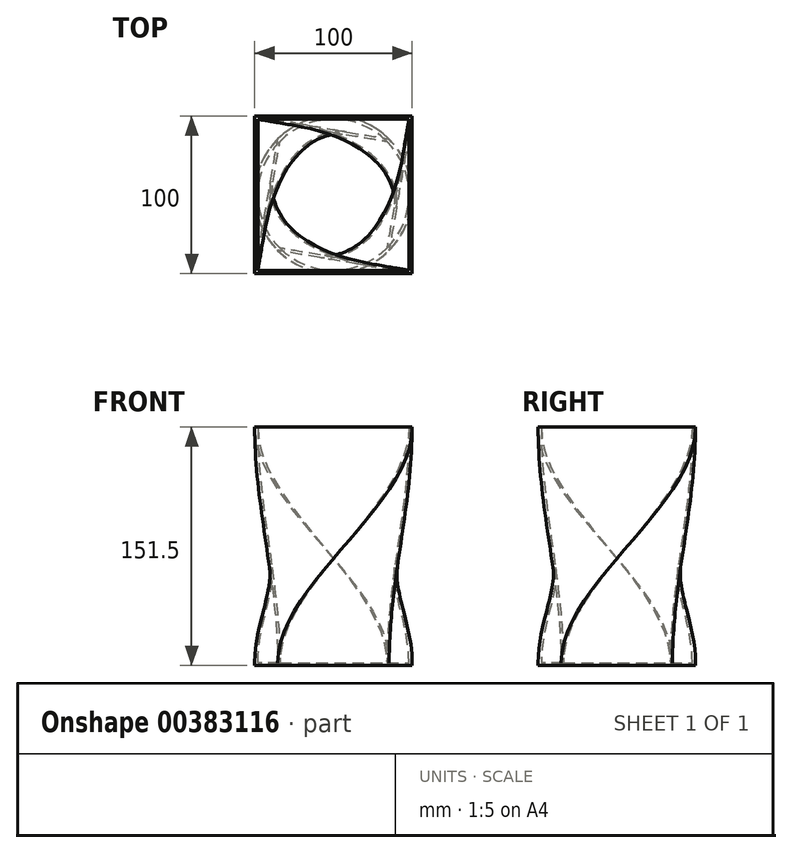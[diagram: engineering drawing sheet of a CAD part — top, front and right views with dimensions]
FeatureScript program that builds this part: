
annotation { "Feature Type Name" : "Feature", "Feature Type Description" : "" }
export const myFeature = defineFeature(function(context is Context, id is Id, definition is map)
    precondition{}
    {
        {
            var Q0;
            Q0=qCreatedBy(makeId("Top.planeOp"),FACE);
            var sketch = newSketch(context, id + "F0", { "sketchPlane" : qUnion([Q0])});
            skArc(sketch, "E0", {"start": v(35.36, 35.36) * mm, "mid": v(0, 50) * mm, "end": v(-35.36, 35.36) * mm});
            skArc(sketch, "E1", {"start": v(35.36, -35.36) * mm, "mid": v(50, 0) * mm, "end": v(35.36, 35.36) * mm});
            skArc(sketch, "E2", {"start": v(-35.36, -35.36) * mm, "mid": v(0, -50) * mm, "end": v(35.36, -35.36) * mm});
            skArc(sketch, "E3", {"start": v(-35.36, 35.36) * mm, "mid": v(-50, 0) * mm, "end": v(-35.36, -35.36) * mm});
            skLineSegment(sketch, "E4", {"start": v(0, 0) * mm, "end": v(51.34, 51.34) * mm, "construction": true});
            skLineSegment(sketch, "E5", {"start": v(0, 0) * mm, "end": v(45.23, -45.23) * mm, "construction": true});
            skLineSegment(sketch, "E6", {"start": v(0, 0) * mm, "end": v(-35.36, -35.36) * mm, "construction": true});
            skLineSegment(sketch, "E7", {"start": v(0, 0) * mm, "end": v(-35.36, 35.36) * mm, "construction": true});
            skSolve(sketch);
        }
        {
            var Q0;
            Q0=qCreatedBy(makeId("Top.planeOp"),FACE);
            cPlane(context, id + "F1", {"entities" : qUnion([Q0]), "cplaneType" : CPlaneType.OFFSET, "offset" : 150 * mm, "width" : 152.4 * mm, "height" : 152.4 * mm});
        }
        {
            var Q0;
            Q0=qCreatedBy(id+"F1.planeOp",FACE);
            var sketch = newSketch(context, id + "F2", { "sketchPlane" : qUnion([Q0])});
            skLineSegment(sketch, "E8.bottom", {"start": v(-50, 50) * mm, "end": v(50, 50) * mm});
            skLineSegment(sketch, "E8.top", {"start": v(-50, -50) * mm, "end": v(50, -50) * mm});
            skLineSegment(sketch, "E8.left", {"start": v(-50, 50) * mm, "end": v(-50, -50) * mm});
            skLineSegment(sketch, "E8.right", {"start": v(50, 50) * mm, "end": v(50, -50) * mm});
            skPoint(sketch, "E8.middle", {"position": v(0, 0) * mm});
            skSolve(sketch);
        }
        {
            var Q0;
            Q0=makeQuery(id+"F2.imprint","IMPRINT",FACE,{"disambiguationData":[TD([[makeQuery(id+"F2.imprint","IMPRINT",EDGE,{"derivedFrom":sQuery(id+"F2.wireOp",EDGE,"E8.bottom")}),-1.0]])]});
            var Q1;
            Q1=makeQuery(id+"F0.imprint","IMPRINT",FACE,{"disambiguationData":[TD([[makeQuery(id+"F0.imprint","IMPRINT",EDGE,{"derivedFrom":sQuery(id+"F0.wireOp",EDGE,"E0")}),1.0]])]});
            var Q2;
            Q2=sQuery(id+"F0.wireOp",VERTEX,"E6.end");
            var Q3;
            Q3=sQuery(id+"F2.wireOp",VERTEX,"E8.top.end");
            loft(context, id + "F3", {"startCondition" : LoftEndDerivativeType.NORMAL_TO_PROFILE, "startMagnitude" : 1, "endCondition" : LoftEndDerivativeType.NORMAL_TO_PROFILE, "endMagnitude" : 1, "sheetProfilesArray" : [{ "sheetProfileEntities" : qUnion([Q0]) }, { "sheetProfileEntities" : qUnion([Q1]) }], "matchConnections" : true, "connections" : [{ "connectionEntities" : qUnion([Q2, Q3]), "connectionEdgeQueries" : qUnion([]), "connectionEdgeParameters" : [] }]});
        }
        {
            var Q0;
            Q0=qCreatedBy(makeId("Top.planeOp"),FACE);
            var sketch = newSketch(context, id + "F4", { "sketchPlane" : qUnion([Q0])});
            skArc(sketch, "E9", {"start": v(33.94, 33.94) * mm, "mid": v(-33.94, 33.94) * mm, "end": v(-33.94, -33.94) * mm});
            skArc(sketch, "E10", {"start": v(33.94, -33.94) * mm, "mid": v(48, 0) * mm, "end": v(33.94, 33.94) * mm});
            skArc(sketch, "E11", {"start": v(-33.94, -33.94) * mm, "mid": v(0, -48) * mm, "end": v(33.94, -33.94) * mm});
            skArc(sketch, "E12", {"start": v(-33.94, 33.94) * mm, "mid": v(-48, 0) * mm, "end": v(-33.94, -33.94) * mm});
            skSolve(sketch);
        }
        {
            var Q0;
            Q0=makeQuery(id+"F2.imprint","IMPRINT",FACE,{"disambiguationData":[TD([[makeQuery(id+"F2.imprint","IMPRINT",EDGE,{"derivedFrom":sQuery(id+"F2.wireOp",EDGE,"E8.bottom")}),-1.0]])]});
            var sketch = newSketch(context, id + "F5", { "sketchPlane" : qUnion([Q0])});
            skLineSegment(sketch, "E13.bottom", {"start": v(-48, 48) * mm, "end": v(48, 48) * mm});
            skLineSegment(sketch, "E13.top", {"start": v(-48, -48) * mm, "end": v(48, -48) * mm});
            skLineSegment(sketch, "E13.left", {"start": v(-48, 48) * mm, "end": v(-48, -48) * mm});
            skLineSegment(sketch, "E13.right", {"start": v(48, 48) * mm, "end": v(48, -48) * mm});
            skPoint(sketch, "E13.middle", {"position": v(0, 0) * mm});
            skSolve(sketch);
        }
        {
            var Q0;
            Q0=makeQuery(id+"F5.imprint","IMPRINT",FACE,{"disambiguationData":[TD([[makeQuery(id+"F5.imprint","IMPRINT",EDGE,{"derivedFrom":sQuery(id+"F5.wireOp",EDGE,"E13.bottom")}),-1.0]])]});
            var Q1;
            Q1=makeQuery(id+"F4.imprint","IMPRINT",FACE,{"disambiguationData":[TD([[makeQuery(id+"F4.imprint","IMPRINT",EDGE,{"derivedFrom":sQuery(id+"F4.wireOp",EDGE,"E9")}),1.0]])]});
            var Q2;
            Q2=sQuery(id+"F4.wireOp",VERTEX,"E12.end");
            var Q3;
            Q3=sQuery(id+"F5.wireOp",VERTEX,"E13.top.end");
            loft(context, id + "F6", {"operationType" : NewBodyOperationType.REMOVE, "startCondition" : LoftEndDerivativeType.NORMAL_TO_PROFILE, "startMagnitude" : 1, "endCondition" : LoftEndDerivativeType.NORMAL_TO_PROFILE, "endMagnitude" : 1, "sheetProfilesArray" : [{ "sheetProfileEntities" : qUnion([Q0]) }, { "sheetProfileEntities" : qUnion([Q1]) }], "matchConnections" : true, "connections" : [{ "connectionEntities" : qUnion([Q2, Q3]), "connectionEdgeQueries" : qUnion([]), "connectionEdgeParameters" : [] }]});
        }
        {
            var Q0;
            Q0=makeQuery(id+"F4.imprint","IMPRINT",FACE,{"disambiguationData":[TD([[makeQuery(id+"F4.imprint","IMPRINT",EDGE,{"derivedFrom":sQuery(id+"F4.wireOp",EDGE,"E9")}),1.0]])]});
            var Q1;
            Q1=makeQuery(id+"F0.imprint","IMPRINT",FACE,{"disambiguationData":[TD([[makeQuery(id+"F0.imprint","IMPRINT",EDGE,{"derivedFrom":sQuery(id+"F0.wireOp",EDGE,"E0")}),1.0]])]});
            extrude(context, id + "F7", {"entities" : qUnion([Q0, Q1]), "operationType" : NewBodyOperationType.ADD, "oppositeDirection" : true, "depth" : 1.5 * mm});
        }
    });
